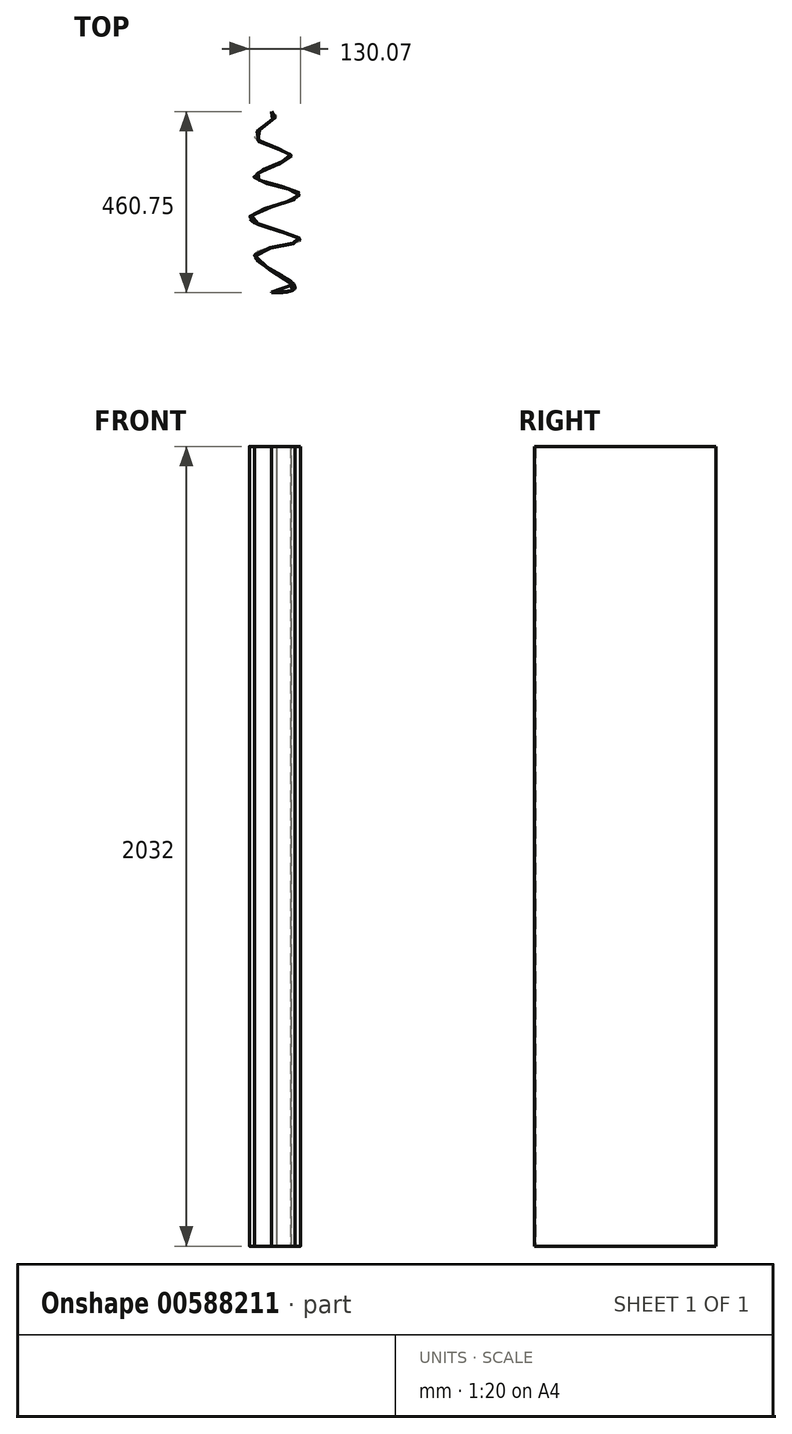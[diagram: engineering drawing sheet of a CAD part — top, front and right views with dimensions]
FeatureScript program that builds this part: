
annotation { "Feature Type Name" : "Feature", "Feature Type Description" : "" }
export const myFeature = defineFeature(function(context is Context, id is Id, definition is map)
    precondition{}
    {
        {
            var Q0;
            Q0=qCreatedBy(makeId("Top.planeOp"),FACE);
            var sketch = newSketch(context, id + "F0", { "sketchPlane" : qUnion([Q0])});
            skLineSegment(sketch, "E0", {"start": v(0, 0) * mm, "end": v(0, 457.2) * mm, "construction": true});
            skFitSpline(sketch, "E1", {"points": [v(0, 457.2) * mm, v(-42.45, 398.97) * mm, v(48.53, 347.72) * mm, v(-44.9, 293.57) * mm, v(71.06, 247.33) * mm, v(-56.13, 188.3) * mm, v(71.6, 131.31) * mm, v(-38.69, 80.85) * mm, v(0, 0) * mm], "startDerivative": vector(1282.53, -77.07) * mm, "endDerivative": vector(-3714.54, 0) * mm});
            skFitSpline(sketch, "E2.0", {"points": [v(0.1, 458.97) * mm, v(1.82, 458.87) * mm, v(4.89, 458.57) * mm, v(8.53, 457.82) * mm, v(10.87, 456.92) * mm, v(12.37, 455.97) * mm, v(13.31, 455.1) * mm, v(14.03, 454.06) * mm, v(14.46, 452.89) * mm, v(14.58, 451.67) * mm, v(14.42, 450.47) * mm, v(14.06, 449.32) * mm, v(13.34, 447.82) * mm, v(12.07, 445.97) * mm, v(10.04, 443.7) * mm, v(7.56, 441.32) * mm, v(4.68, 438.84) * mm, v(0.4, 435.4) * mm, v(-5.63, 430.89) * mm, v(-13.41, 425.21) * mm, v(-21.2, 419.4) * mm, v(-27.25, 414.54) * mm, v(-31.53, 410.72) * mm, v(-34.4, 407.91) * mm, v(-36.84, 405.19) * mm, v(-38.8, 402.57) * mm, v(-39.96, 400.52) * mm, v(-40.6, 398.99) * mm, v(-41.02, 397.54) * mm, v(-41.2, 395.84) * mm, v(-40.93, 393.9) * mm, v(-40.18, 391.99) * mm, v(-38.94, 390.06) * mm, v(-37.2, 388.14) * mm, v(-34.26, 385.6) * mm, v(-29.52, 382.54) * mm, v(-22.47, 379.06) * mm, v(-14.4, 375.79) * mm, v(-5.65, 372.7) * mm, v(3.44, 369.75) * mm, v(12.55, 366.93) * mm, v(21.36, 364.19) * mm, v(29.55, 361.49) * mm, v(35.6, 359.23) * mm, v(39.84, 357.4) * mm, v(42.67, 356) * mm, v(45.13, 354.55) * mm, v(47.2, 353.03) * mm, v(48.57, 351.66) * mm, v(49.43, 350.45) * mm, v(49.92, 349.48) * mm, v(50.25, 348.43) * mm, v(50.37, 347.33) * mm, v(50.27, 346.24) * mm, v(49.89, 344.84) * mm, v(49.01, 343.22) * mm, v(47.48, 341.41) * mm, v(45.52, 339.67) * mm, v(43.17, 337.95) * mm, v(40.44, 336.23) * mm, v(36.36, 333.93) * mm, v(30.5, 331.02) * mm, v(22.5, 327.49) * mm, v(13.86, 323.91) * mm, v(4.85, 320.31) * mm, v(-4.22, 316.7) * mm, v(-13.05, 313.09) * mm, v(-21.34, 309.5) * mm, v(-28.77, 305.96) * mm, v(-33.99, 303.08) * mm, v(-37.4, 300.85) * mm, v(-39.55, 299.22) * mm, v(-41.23, 297.66) * mm, v(-42.4, 296.2) * mm, v(-42.92, 295.16) * mm, v(-43.11, 294.43) * mm, v(-43.16, 293.94) * mm, v(-43.12, 293.47) * mm, v(-42.94, 292.81) * mm, v(-42.45, 291.87) * mm, v(-41.3, 290.58) * mm, v(-39.6, 289.21) * mm, v(-37.4, 287.81) * mm, v(-34.75, 286.4) * mm, v(-31.68, 285) * mm, v(-27.09, 283.15) * mm, v(-20.52, 280.85) * mm, v(-11.61, 278.15) * mm, v(-1.97, 275.5) * mm, v(8.11, 272.87) * mm, v(18.36, 270.28) * mm, v(28.49, 267.7) * mm, v(38.21, 265.13) * mm, v(47.26, 262.54) * mm, v(54, 260.37) * mm, v(58.8, 258.6) * mm, v(62.06, 257.26) * mm, v(64.96, 255.9) * mm, v(67.47, 254.5) * mm, v(69.57, 253.03) * mm, v(70.96, 251.73) * mm, v(71.84, 250.57) * mm, v(72.36, 249.65) * mm, v(72.72, 248.64) * mm, v(72.87, 247.57) * mm, v(72.8, 246.48) * mm, v(72.5, 245.45) * mm, v(72.03, 244.49) * mm, v(71.22, 243.28) * mm, v(69.9, 241.89) * mm, v(67.86, 240.3) * mm, v(65.4, 238.75) * mm, v(62.54, 237.2) * mm, v(59.3, 235.66) * mm, v(54.5, 233.6) * mm, v(47.7, 231) * mm, v(38.5, 227.82) * mm, v(28.52, 224.6) * mm, v(18.03, 221.35) * mm, v(7.3, 218.04) * mm, v(-3.4, 214.7) * mm, v(-13.8, 211.3) * mm, v(-23.64, 207.89) * mm, v(-32.61, 204.45) * mm, v(-40.45, 201) * mm, v(-45.8, 198.12) * mm, v(-49.2, 195.85) * mm, v(-51.29, 194.18) * mm, v(-52.85, 192.58) * mm, v(-53.88, 191.08) * mm, v(-54.3, 189.96) * mm, v(-54.4, 189.15) * mm, v(-54.39, 188.55) * mm, v(-54.27, 187.94) * mm, v(-53.95, 187.06) * mm, v(-53.22, 185.84) * mm, v(-51.78, 184.24) * mm, v(-49.8, 182.55) * mm, v(-47.3, 180.83) * mm, v(-43.35, 178.5) * mm, v(-37.36, 175.55) * mm, v(-28.82, 172.02) * mm, v(-19.22, 168.51) * mm, v(-8.85, 165.04) * mm, v(1.98, 161.62) * mm, v(13, 158.27) * mm, v(23.9, 155) * mm, v(34.41, 151.8) * mm, v(44.25, 148.7) * mm, v(51.65, 146.2) * mm, v(56.95, 144.27) * mm, v(60.58, 142.84) * mm, v(63.84, 141.43) * mm, v(66.7, 140.05) * mm, v(69.13, 138.68) * mm, v(71.12, 137.3) * mm, v(72.41, 136.08) * mm, v(73.2, 134.99) * mm, v(73.64, 134.08) * mm, v(73.88, 133.07) * mm, v(73.85, 132) * mm, v(73.51, 130.97) * mm, v(72.94, 130.08) * mm, v(72.22, 129.32) * mm, v(71.37, 128.66) * mm, v(70.41, 128.06) * mm, v(68.97, 127.3) * mm, v(66.86, 126.42) * mm, v(63.85, 125.4) * mm, v(60.4, 124.43) * mm, v(56.52, 123.47) * mm, v(52.28, 122.52) * mm, v(46.2, 121.26) * mm, v(37.86, 119.67) * mm, v(27.1, 117.7) * mm, v(15.93, 115.6) * mm, v(4.73, 113.33) * mm, v(-6.12, 110.85) * mm, v(-16.24, 108.1) * mm, v(-25.24, 105.06) * mm, v(-31.47, 102.25) * mm, v(-35.48, 99.84) * mm, v(-37.96, 97.98) * mm, v(-39.85, 96.07) * mm, v(-41.12, 94.16) * mm, v(-41.8, 92.25) * mm, v(-41.94, 90.28) * mm, v(-41.48, 88.1) * mm, v(-40.3, 85.66) * mm, v(-38.63, 83.4) * mm, v(-36.84, 81.47) * mm, v(-34.74, 79.46) * mm, v(-31.58, 76.82) * mm, v(-27.04, 73.5) * mm, v(-21.88, 70.04) * mm, v(-14.3, 65.3) * mm, v(-3.8, 59.16) * mm, v(9.6, 51.64) * mm, v(22.95, 44.1) * mm, v(33.35, 37.94) * mm, v(40.83, 33.14) * mm, v(45.92, 29.63) * mm, v(50.39, 26.2) * mm, v(54.14, 22.87) * mm, v(57.1, 19.62) * mm, v(58.8, 16.94) * mm, v(59.63, 14.74) * mm, v(59.94, 13.05) * mm, v(59.88, 11.34) * mm, v(59.4, 9.69) * mm, v(58.51, 8.16) * mm, v(57.28, 6.79) * mm, v(55.71, 5.57) * mm, v(53.2, 4.1) * mm, v(49.21, 2.54) * mm, v(42.94, 1) * mm, v(35.04, -0.22) * mm, v(25.39, -1.1) * mm, v(13.86, -1.65) * mm, v(4.85, -1.78) * mm, v(0, -1.78) * mm]});
            skLineSegment(sketch, "E3", {"start": v(0, -1.78) * mm, "end": v(0, 0) * mm});
            skLineSegment(sketch, "E4", {"start": v(0.1, 458.97) * mm, "end": v(0, 457.2) * mm});
            skSolve(sketch);
        }
        {
            var Q0;
            Q0 = qSketchRegion(id + "F0", true);
            extrude(context, id + "F1", {"entities" : qUnion([Q0]), "depth" : 2032 * mm, "offsetDistance" : 25.4 * mm});
        }
    });
